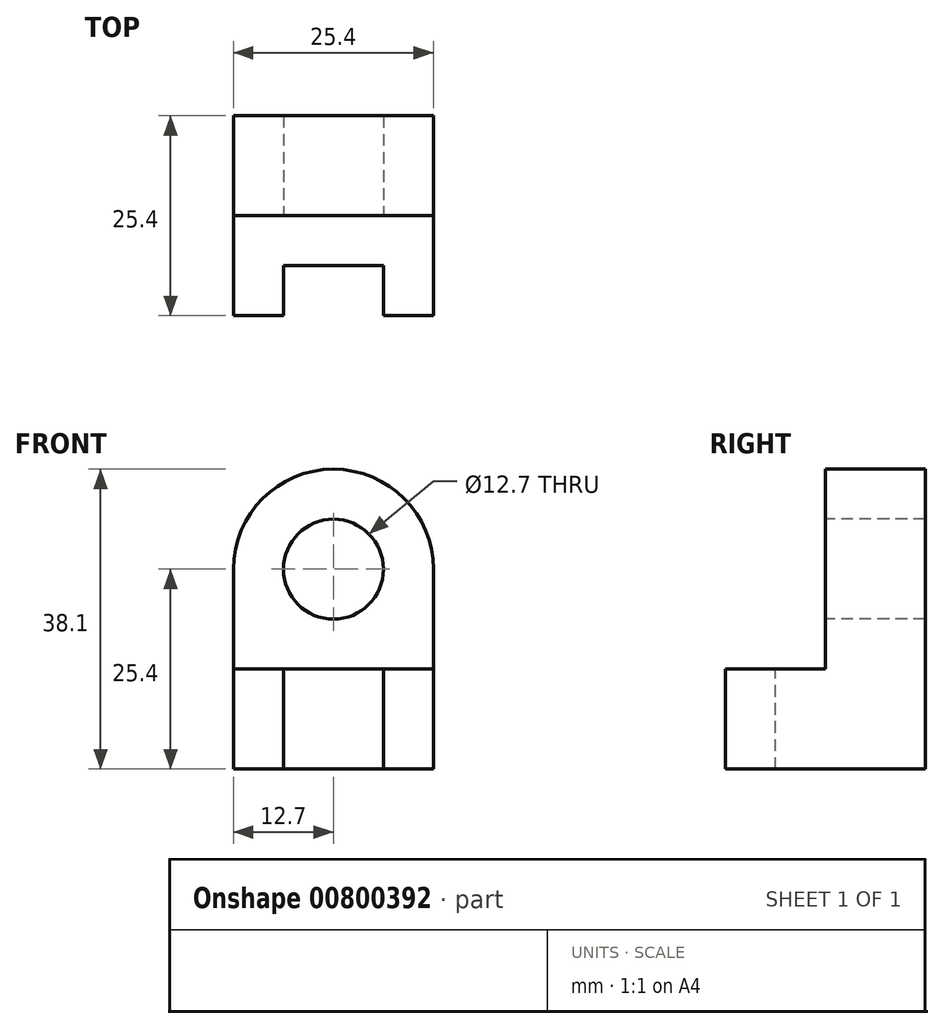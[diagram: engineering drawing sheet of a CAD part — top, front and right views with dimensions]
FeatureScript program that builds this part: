
annotation { "Feature Type Name" : "Feature", "Feature Type Description" : "" }
export const myFeature = defineFeature(function(context is Context, id is Id, definition is map)
    precondition{}
    {
        {
            var Q0;
            Q0=qCreatedBy(makeId("Front.planeOp"),FACE);
            var sketch = newSketch(context, id + "F0", { "sketchPlane" : qUnion([Q0])});
            skLineSegment(sketch, "E0", {"start": v(0, 0) * mm, "end": v(25.4, 0) * mm});
            skLineSegment(sketch, "E1", {"start": v(25.4, 0) * mm, "end": v(25.4, 44.45) * mm});
            skLineSegment(sketch, "E2", {"start": v(25.4, 44.45) * mm, "end": v(0, 44.45) * mm});
            skLineSegment(sketch, "E3", {"start": v(0, 44.45) * mm, "end": v(0, 0) * mm});
            skSolve(sketch);
        }
        {
            var Q0;
            Q0=makeQuery(id+"F0.imprint","IMPRINT",FACE,{"disambiguationData":[TD([[makeQuery(id+"F0.imprint","IMPRINT",EDGE,{"derivedFrom":sQuery(id+"F0.wireOp",EDGE,"E0")}),1.0]])]});
            extrude(context, id + "F1", {"entities" : qUnion([Q0]), "depth" : 25.4 * mm, "offsetDistance" : 25.4 * mm});
        }
        {
            var Q0;
            Q0=makeQuery(id+"F1.opExtrude","SWEPT_FACE",FACE,{"disambiguationData":[OSD([sQuery(id+"F0.wireOp",EDGE,"E1")])]});
            var sketch = newSketch(context, id + "F2", { "sketchPlane" : qUnion([Q0])});
            skLineSegment(sketch, "E4", {"start": v(-25.4, 0) * mm, "end": v(-25.4, 12.7) * mm});
            skLineSegment(sketch, "E5", {"start": v(-25.4, 12.7) * mm, "end": v(-12.7, 12.7) * mm});
            skLineSegment(sketch, "E6", {"start": v(-12.7, 12.7) * mm, "end": v(-12.7, 44.45) * mm});
            skSolve(sketch);
        }
        {
            var Q0;
            {var subQ0=sQuery(id+"F2.wireOp",EDGE,"E5");Q0=makeQuery(id+"F2.imprint","IMPRINT",FACE,{"disambiguationData":[TD([[makeQuery(id+"F2.imprint","IMPRINT",EDGE,{"derivedFrom":subQ0}),1.0]])]});}
            extrude(context, id + "F3", {"entities" : qUnion([Q0]), "operationType" : NewBodyOperationType.REMOVE, "endBound" : BoundingType.THROUGH_ALL, "oppositeDirection" : true, "depth" : 25.4 * mm, "offsetDistance" : 25.4 * mm});
        }
        {
            var Q0;
            Q0=makeQuery(id+"F1.opExtrude","CAP_FACE",FACE,{"disambiguationData":[OSD([sQuery(id+"F0.wireOp",EDGE,"E0"),sQuery(id+"F0.wireOp",EDGE,"E1"),sQuery(id+"F0.wireOp",EDGE,"E2"),sQuery(id+"F0.wireOp",EDGE,"E3")])],"isStart":false});
            var sketch = newSketch(context, id + "F4", { "sketchPlane" : qUnion([Q0])});
            skLineSegment(sketch, "E7", {"start": v(0, 0) * mm, "end": v(6.35, 0) * mm});
            skLineSegment(sketch, "E8", {"start": v(25.4, 0) * mm, "end": v(19.05, 0) * mm});
            skLineSegment(sketch, "E9", {"start": v(19.05, 0) * mm, "end": v(19.05, 12.7) * mm});
            skLineSegment(sketch, "E10", {"start": v(6.35, 0) * mm, "end": v(6.35, 12.7) * mm});
            skSolve(sketch);
        }
        {
            var Q0;
            {var subQ0=sQuery(id+"F4.wireOp",EDGE,"E9");Q0=makeQuery(id+"F4.imprint","IMPRINT",FACE,{"disambiguationData":[TD([[makeQuery(id+"F4.imprint","IMPRINT",EDGE,{"derivedFrom":subQ0}),1.0]])]});}
            extrude(context, id + "F5", {"entities" : qUnion([Q0]), "operationType" : NewBodyOperationType.REMOVE, "oppositeDirection" : true, "depth" : 6.35 * mm, "offsetDistance" : 25.4 * mm});
        }
        {
            var Q0;
            Q0=makeQuery(id+"F3.boolean.opBoolean","COPY",FACE,{"derivedFrom":makeQuery(id+"F3.opExtrude","SWEPT_FACE",FACE,{"disambiguationData":[OSD([sQuery(id+"F2.wireOp",EDGE,"E6")])]})});
            var sketch = newSketch(context, id + "F6", { "sketchPlane" : qUnion([Q0])});
            skLineSegment(sketch, "E11", {"start": v(25.4, 12.7) * mm, "end": v(25.4, 25.4) * mm});
            skLineSegment(sketch, "E12", {"start": v(0, 12.7) * mm, "end": v(0, 25.4) * mm});
            skArc(sketch, "E13", {"start": v(25.4, 25.4) * mm, "mid": v(12.7, 38.1) * mm, "end": v(0, 25.4) * mm});
            skSolve(sketch);
        }
        {
            var Q0;
            {var subQ0=sQuery(id+"F6.wireOp",EDGE,"E13");Q0=makeQuery(id+"F6.imprint","IMPRINT",FACE,{"disambiguationData":[TD([[makeQuery(id+"F6.imprint","IMPRINT",EDGE,{"derivedFrom":subQ0}),-1.0]])]});}
            extrude(context, id + "F7", {"entities" : qUnion([Q0]), "operationType" : NewBodyOperationType.REMOVE, "endBound" : BoundingType.THROUGH_ALL, "oppositeDirection" : true, "depth" : 25.4 * mm, "offsetDistance" : 25.4 * mm});
        }
        {
            var Q0;
            Q0=makeQuery(id+"F3.boolean.opBoolean","COPY",FACE,{"derivedFrom":makeQuery(id+"F3.opExtrude","SWEPT_FACE",FACE,{"disambiguationData":[OSD([sQuery(id+"F2.wireOp",EDGE,"E6")])]})});
            var sketch = newSketch(context, id + "F8", { "sketchPlane" : qUnion([Q0])});
            skLineSegment(sketch, "E14", {"start": v(25.4, 25.4) * mm, "end": v(0, 25.4) * mm, "construction": true});
            skCircle(sketch, "E15", {"center": v(12.7, 25.4) * mm, "radius": 6.35 * mm});
            skSolve(sketch);
        }
        {
            var Q0;
            Q0=makeQuery(id+"F8.imprint","IMPRINT",FACE,{"disambiguationData":[TD([[makeQuery(id+"F8.imprint","IMPRINT",EDGE,{"derivedFrom":sQuery(id+"F8.wireOp",EDGE,"E15")}),1.0]])]});
            extrude(context, id + "F9", {"entities" : qUnion([Q0]), "operationType" : NewBodyOperationType.REMOVE, "oppositeDirection" : true, "depth" : 25.4 * mm, "offsetDistance" : 25.4 * mm});
        }
    });
